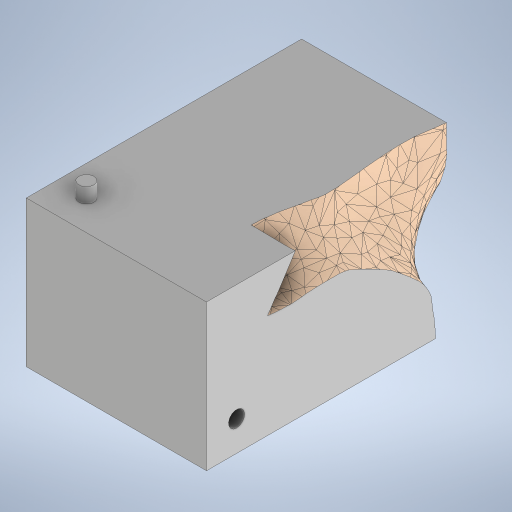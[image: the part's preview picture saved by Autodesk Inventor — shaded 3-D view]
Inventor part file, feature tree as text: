
AUTODESK INVENTOR PART (.ipt)
format: ipt  version: 2024 (Build 280153000, 153)  size: 10,765,824 bytes
history: native  units: mm
features: other x6, extrude x6, sketch x6, plane x2
ambient origin geometry x8: Origin, YZ Plane, XZ Plane, XY Plane, X Axis, Y Axis, Z Axis, Center Point
bodies: Body1 (feature_tree)
feature tree (20):
  other  "M.ipt"
  plane  "Plano de trabajo1"
  extrude  "Extrusión1"  [1 undecoded]
  other  "Combinar1"
  sketch  "Boceto3"  dims[d2=550.0mm d3=520.0mm]
  sketch  "Boceto4"  dims[d4=550.0mm d5=0.0mm d6=129.8482mm]
  plane  "Plano de trabajo2"
  sketch  "Boceto5"  dims[d17=180.0mm d18=180.0mm]
  extrude  "Extrusión2"  Depth=520.0mm
  extrude  "Extrusión3"  Depth=129.8482mm
  extrude  "Extrusión4"  Depth=180.0mm
  extrude  "Extrusión5"  Depth=180.0mm
  extrude  "Extrusión6"  Depth=180.0mm
  other  "Sólido1::M.ipt"
  other  "OperaciónIdentificador1"
  sketch  "Boceto1"  dims[d0=25.0mm d1=-365.0mm]
  other  "Sólido2"
  sketch  "Boceto6"  dims[d22=326.0mm d23=180.0mm]
  sketch  "Boceto7"  dims[d24=180.0mm d25=180.0mm d26=10.0mm d27=0.0mm d28=1000.0mm d29=0.0mm d30=1000.0mm d31=0.0mm d32=30.0mm d33=30.0mm d34=15.0mm d35=15.0mm d36=161.0mm d37=0.0mm d38=0.0mm d39=30.0mm d40=30.0mm d41=16.0mm d42=16.0mm d43=0.0mm d14=0.5mm d15=0.872665mm d16=0.5mm d19=0.5mm d20=0.872665mm d21=0.5mm]
  other  "Sólido1"
note: 1 required parameter value undecoded (feature->parameter linkage not recoverable at this tier; creation-order binding heuristic only, values carry confidence <= 0.55)
